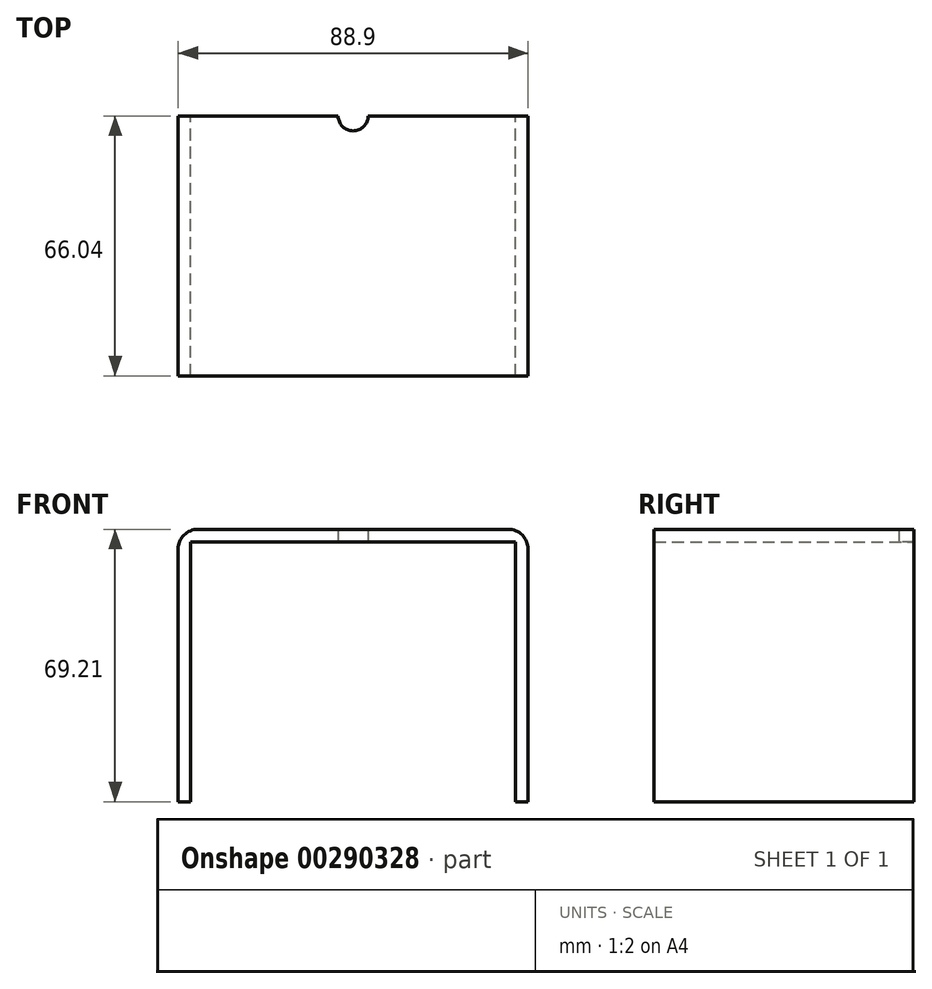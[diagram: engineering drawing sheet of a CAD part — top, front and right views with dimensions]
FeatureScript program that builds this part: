
annotation { "Feature Type Name" : "Feature", "Feature Type Description" : "" }
export const myFeature = defineFeature(function(context is Context, id is Id, definition is map)
    precondition{}
    {
        {
            var Q0;
            Q0=qCreatedBy(makeId("Top.planeOp"),FACE);
            var sketch = newSketch(context, id + "F0", { "sketchPlane" : qUnion([Q0])});
            skLineSegment(sketch, "E0.bottom", {"start": v(44.45, 33.02) * mm, "end": v(-44.45, 33.02) * mm});
            skLineSegment(sketch, "E0.top", {"start": v(44.45, -33.02) * mm, "end": v(-44.45, -33.02) * mm});
            skLineSegment(sketch, "E0.left", {"start": v(44.45, 33.02) * mm, "end": v(44.45, -33.02) * mm});
            skLineSegment(sketch, "E0.right", {"start": v(-44.45, 33.02) * mm, "end": v(-44.45, -33.02) * mm});
            skPoint(sketch, "E0.middle", {"position": v(0, 0) * mm});
            skLineSegment(sketch, "E1", {"start": v(-41.28, -33.02) * mm, "end": v(-41.28, 33.02) * mm});
            skLineSegment(sketch, "E2", {"start": v(41.28, -33.02) * mm, "end": v(41.28, 33.02) * mm});
            skArc(sketch, "E3", {"start": v(-3.81, 33.02) * mm, "mid": v(0, 29.21) * mm, "end": v(3.81, 33.02) * mm});
            skSolve(sketch);
        }
        {
            var Q0;
            {var subQ0=sQuery(id+"F0.wireOp",EDGE,"E0.left");Q0=makeQuery(id+"F0.imprint","IMPRINT",FACE,{"disambiguationData":[TD([[makeQuery(id+"F0.imprint","IMPRINT",EDGE,{"derivedFrom":subQ0}),-1.0]])]});}
            var Q1;
            {var subQ0=sQuery(id+"F0.wireOp",EDGE,"E0.right");Q1=makeQuery(id+"F0.imprint","IMPRINT",FACE,{"disambiguationData":[TD([[makeQuery(id+"F0.imprint","IMPRINT",EDGE,{"derivedFrom":subQ0}),1.0]])]});}
            var Q2;
            {var subQ0=sQuery(id+"F0.wireOp",EDGE,"E1");Q2=makeQuery(id+"F0.imprint","IMPRINT",FACE,{"disambiguationData":[TD([[makeQuery(id+"F0.imprint","IMPRINT",EDGE,{"derivedFrom":subQ0}),-1.0]])]});}
            extrude(context, id + "F1", {"entities" : qUnion([Q0, Q1, Q2]), "depth" : 3.17 * mm});
        }
        {
            var Q0;
            {var subQ0=sQuery(id+"F0.wireOp",EDGE,"E0.right");Q0=makeQuery(id+"F0.imprint","IMPRINT",FACE,{"disambiguationData":[TD([[makeQuery(id+"F0.imprint","IMPRINT",EDGE,{"derivedFrom":subQ0}),1.0]])]});}
            var Q1;
            {var subQ0=sQuery(id+"F0.wireOp",EDGE,"E0.left");Q1=makeQuery(id+"F0.imprint","IMPRINT",FACE,{"disambiguationData":[TD([[makeQuery(id+"F0.imprint","IMPRINT",EDGE,{"derivedFrom":subQ0}),-1.0]])]});}
            extrude(context, id + "F2", {"entities" : qUnion([Q0, Q1]), "operationType" : NewBodyOperationType.ADD, "oppositeDirection" : true, "depth" : 66.04 * mm});
        }
        {
            var Q0;
            Q0=makeQuery(id+"F1.opExtrude","CAP_EDGE",EDGE,{"disambiguationData":[OSD([sQuery(id+"F0.wireOp",EDGE,"E0.right")])],"isStart":false});
            var Q1;
            Q1=makeQuery(id+"F1.opExtrude","CAP_EDGE",EDGE,{"disambiguationData":[OSD([sQuery(id+"F0.wireOp",EDGE,"E0.left")])],"isStart":false});
            fillet(context, id + "F3", {"entities" : qUnion([Q0, Q1]), "radius" : 5.08 * mm, "tangentPropagation" : true, "allowEdgeOverflow" : false});
        }
    });
